# Revit family: dl_vario_quattro_pro_led_057596
name_source: partatom
category: Leuchten
revit_build: Autodesk Revit 2016 (Build: 20190508_0715(x64)
units: mm (PartAtom-declared; Revit-internal decimal feet)

## family parameters
Basisbauteil = Fläche
Beim Laden mit Abzugskörper schneiden = Nein
Bemaßung runder Anschluss = Durchmesser verwenden
Gemeinsam genutzt = Nein
Lichtquelle = Nein
Raumberechnungspunkt = Nein
Teiletyp = Normal

## types (1)
- DL Vario Quattro PRO LED (1 x , 1430 lm, 3000 K)
    Beschreibung = Dimensions (Ø x H): 310 x 69 mm; Mains power supply: 220 – 240 V / 50 – 60 Hz; Mounting height max.: 6,00 m; Sensor Technology: passive infrared; Output: 14 W; Interconnection: Yes; Type of interconnection: Master/master; Slave modeselectable: No; Interconnection, number: 10 lights max.; Luminous flux: 1430 lm; Colour temperature: 3000 K; Colour variation LED: SDCM3; Colour Rendering Index CRI: 80-89; With lamp: Yes, STEINEL LED system; Lamp: LED cannot be replaced; LED life expectancy (max. °C): 50000 h; Base: without; LED cooling system: Passive Thermo Control; With motion detector: Yes; Detection angle: 360 °; Angle of aperture: 180 °; Sneak-by guard: Yes; Capability of masking out individual segments: No; Electronic scalability: No; Mechanical scalability: Yes; Reach, detail: Reach adjustable from 2 - 8 m in 4 directions (90° in each); Reach, radial: 6 x 6 m (36 m²); Reach, tangential: 16 x 16 m (256 m²); Photo-cell controller: Yes; Twilight setting: 2 – 1000 lx; Time setting: 5 sec – 30 min; Basic light level function: Yes; Basic light level function time: 10/30 min, all night; Soft light start: Yes; Continuous light: selectable, 4h; Impact resistance: IK07; IP-rating: IP54; Protection class: II; Ambient temperature: -20 – 35 °C; Housing material: Plastic; Cover material: Plastic, structured; Manufacturer's Warranty: 5 years; Settings via: Potentiometers; With remote control: No; Version: warm white anthracite; PU1, EAN: 4007841057596
    Color Rendering = 80-89
    Color Temperature = 3000 K
    Frequency = 60 Hz, 50 Hz
    Height = 0 mm  [stored 0 ft]
    Hersteller = Steinel
    Lamp Light Flux = 1430 lm
    Lamp count = 1
    Lampe = 1 x
    Length = 310 mm
    Luminous efficacy = 0 lm/W
    ModVariant = Nein
    Modell = 057596
    Mounting Place = Ceiling
    Mounting Type = Surface mounted
    Number of Poles = 1
    OnlyDefault = Ja
    Power Factor = 1
    Product Name = DL Vario Quattro PRO LED
    Product group = Sensor-switched outdoor light
    ProductGroupID = 3
    Protection Class = Protection class II
    Protection Degree = IP 54
    RlxData = <blob elided: 50753 chars, md5=a690adc4>
    Scheinlast = 14 VA
    Socket = socket
    Standby Power = 0 W
    System Light Flux = 0 lm
    System Power = 14 W
    Typenbild = produkt1_057596.jpg
    Typenkommentare = Product without accessories
    URL = http://relux.com
    VarID = ---
    Voltage = 0 V
    Vorgabe-Ansicht = 1800 mm
    Weight = 0.00 kg
    Width = 0 mm  [stored 0 ft]

note: [stored X ft] marks values corroborated as IEEE doubles in the binary element streams (Revit-internal decimal feet)

## geometry (parser evidence)
native form markers: Blend x4, Sweep x9
no freeform markers — native parametric forms only
